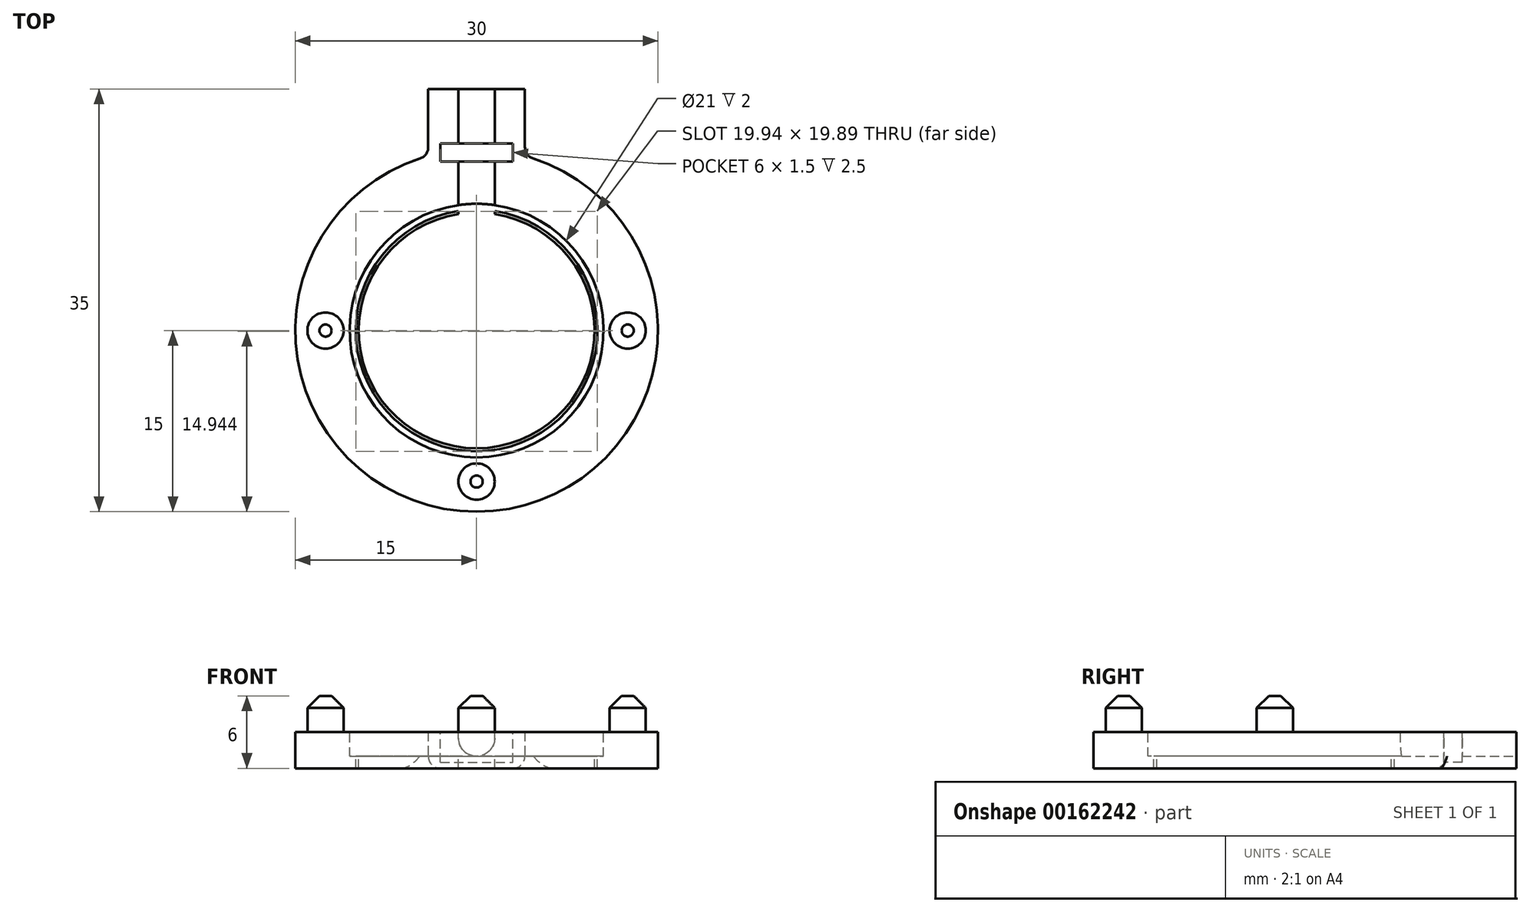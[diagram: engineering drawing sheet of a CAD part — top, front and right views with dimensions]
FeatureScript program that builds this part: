
annotation { "Feature Type Name" : "Feature", "Feature Type Description" : "" }
export const myFeature = defineFeature(function(context is Context, id is Id, definition is map)
    precondition{}
    {
        {
            var Q0;
            Q0=qCreatedBy(makeId("Top.planeOp"),FACE);
            var sketch = newSketch(context, id + "F0", { "sketchPlane" : qUnion([Q0])});
            skArc(sketch, "E0", {"start": v(-4, 14.46) * mm, "mid": v(0, -15) * mm, "end": v(4, 14.46) * mm});
            skLineSegment(sketch, "E1.bottom", {"start": v(-4, 20) * mm, "end": v(4, 20) * mm});
            skLineSegment(sketch, "E1.left", {"start": v(-4, 20) * mm, "end": v(-4, 14.46) * mm});
            skLineSegment(sketch, "E1.right", {"start": v(4, 20) * mm, "end": v(4, 14.46) * mm});
            skSolve(sketch);
        }
        {
            var Q0;
            Q0 = qSketchRegion(id + "F0", true);
            extrude(context, id + "F1", {"entities" : qUnion([Q0]), "depth" : 3 * mm});
        }
        {
            var Q0;
            Q0=makeQuery(id+"F1.opExtrude","CAP_FACE",FACE,{"disambiguationData":[OSD([sQuery(id+"F0.wireOp",EDGE,"E0"),sQuery(id+"F0.wireOp",EDGE,"E1.bottom"),sQuery(id+"F0.wireOp",EDGE,"E1.left"),sQuery(id+"F0.wireOp",EDGE,"E1.right")])],"isStart":false});
            var sketch = newSketch(context, id + "F2", { "sketchPlane" : qUnion([Q0])});
            skLineSegment(sketch, "E2.bottom", {"start": v(-1.5, 20) * mm, "end": v(1.5, 20) * mm});
            skLineSegment(sketch, "E2.left", {"start": v(-1.5, 20) * mm, "end": v(-1.5, 10.4) * mm});
            skLineSegment(sketch, "E2.right", {"start": v(1.5, 20) * mm, "end": v(1.5, 10.4) * mm});
            skArc(sketch, "E3", {"start": v(-1.5, 10.4) * mm, "mid": v(0, -10.5) * mm, "end": v(1.5, 10.4) * mm});
            skPoint(sketch, "E4.orphan", {"position": v(1.5, 8.67) * mm});
            skSolve(sketch);
        }
        {
            var Q0;
            Q0 = qSketchRegion(id + "F2", true);
            extrude(context, id + "F3", {"entities" : qUnion([Q0]), "operationType" : NewBodyOperationType.REMOVE, "oppositeDirection" : true, "depth" : 2 * mm});
        }
        {
            var Q0;
            Q0=makeQuery(id+"F1.opExtrude","CAP_FACE",FACE,{"disambiguationData":[OSD([sQuery(id+"F0.wireOp",EDGE,"E0"),sQuery(id+"F0.wireOp",EDGE,"E1.bottom"),sQuery(id+"F0.wireOp",EDGE,"E1.left"),sQuery(id+"F0.wireOp",EDGE,"E1.right")])],"isStart":false});
            var sketch = newSketch(context, id + "F4", { "sketchPlane" : qUnion([Q0])});
            skCircle(sketch, "E5", {"center": v(12.5, 0) * mm, "radius": 1.5 * mm});
            skCircle(sketch, "E6", {"center": v(-12.5, 0) * mm, "radius": 1.5 * mm});
            skCircle(sketch, "E7", {"center": v(0, -12.5) * mm, "radius": 1.5 * mm});
            skSolve(sketch);
        }
        {
            var Q0;
            Q0 = qSketchRegion(id + "F4", true);
            extrude(context, id + "F5", {"entities" : qUnion([Q0]), "operationType" : NewBodyOperationType.ADD, "depth" : 3 * mm});
        }
        {
            var Q0;
            Q0=makeQuery(id+"F5.opExtrude","CAP_EDGE",EDGE,{"disambiguationData":[OSD([sQuery(id+"F4.wireOp",EDGE,"E6")])],"isStart":false});
            var Q1;
            Q1=makeQuery(id+"F5.opExtrude","CAP_EDGE",EDGE,{"disambiguationData":[OSD([sQuery(id+"F4.wireOp",EDGE,"E7")])],"isStart":false});
            var Q2;
            Q2=makeQuery(id+"F5.opExtrude","CAP_EDGE",EDGE,{"disambiguationData":[OSD([sQuery(id+"F4.wireOp",EDGE,"E5")])],"isStart":false});
            chamfer(context, id + "F6", {"entities" : qUnion([Q0, Q1, Q2]), "width" : 1 * mm, "tangentPropagation" : true});
        }
        {
            var Q0;
            Q0=makeQuery(id+"F1.opExtrude","CAP_EDGE",EDGE,{"disambiguationData":[OSD([sQuery(id+"F0.wireOp",EDGE,"E1.right")])],"isStart":true});
            var Q1;
            Q1=makeQuery(id+"F1.opExtrude","SWEPT_EDGE",EDGE,{"disambiguationData":[OSD([sQuery(id+"F0.wireOp",EDGE,"E0"),sQuery(id+"F0.wireOp",EDGE,"E1.right")])]});
            var Q2;
            Q2=makeQuery(id+"F1.opExtrude","SWEPT_EDGE",EDGE,{"disambiguationData":[OSD([sQuery(id+"F0.wireOp",EDGE,"E0"),sQuery(id+"F0.wireOp",EDGE,"E1.left")])]});
            var Q3;
            Q3=makeQuery(id+"F1.opExtrude","CAP_EDGE",EDGE,{"disambiguationData":[OSD([sQuery(id+"F0.wireOp",EDGE,"E1.left")])],"isStart":true});
            fillet(context, id + "F7", {"entities" : qUnion([Q0, Q1, Q2, Q3]), "radius" : 1 * mm, "tangentPropagation" : true, "allowEdgeOverflow" : false});
        }
        {
            var Q0;
            Q0=makeQuery(id+"F3.boolean.opBoolean","COPY",FACE,{"derivedFrom":makeQuery(id+"F3.opExtrude","CAP_FACE",FACE,{"disambiguationData":[OSD([sQuery(id+"F2.wireOp",EDGE,"E2.bottom"),sQuery(id+"F2.wireOp",EDGE,"E2.left"),sQuery(id+"F2.wireOp",EDGE,"E2.right"),sQuery(id+"F2.wireOp",EDGE,"E3")])],"isStart":false})});
            var sketch = newSketch(context, id + "F8", { "sketchPlane" : qUnion([Q0])});
            skArc(sketch, "E8", {"start": v(-1.5, 9.89) * mm, "mid": v(0, -10) * mm, "end": v(1.5, 9.89) * mm});
            skArc(sketch, "E9", {"start": v(-1.5, 9.63) * mm, "mid": v(0, -9.75) * mm, "end": v(1.5, 9.63) * mm});
            skLineSegment(sketch, "E10.left", {"start": v(-1.5, 9.89) * mm, "end": v(-1.5, 9.63) * mm});
            skLineSegment(sketch, "E10.right", {"start": v(1.5, 9.89) * mm, "end": v(1.5, 9.63) * mm});
            skPoint(sketch, "E11.orphan", {"position": v(1.5, 7.73) * mm});
            skSolve(sketch);
        }
        {
            var Q0;
            Q0 = qSketchRegion(id + "F8", true);
            extrude(context, id + "F9", {"entities" : qUnion([Q0]), "operationType" : NewBodyOperationType.REMOVE, "endBound" : BoundingType.THROUGH_ALL, "oppositeDirection" : true, "depth" : 25 * mm});
        }
        {
            var Q0;
            Q0=makeQuery(id+"F3.boolean.opBoolean","COPY",EDGE,{"derivedFrom":makeQuery(id+"F3.opExtrude","CAP_EDGE",EDGE,{"disambiguationData":[OSD([sQuery(id+"F2.wireOp",EDGE,"E2.right")])],"isStart":false})});
            var Q1;
            Q1=makeQuery(id+"F3.boolean.opBoolean","COPY",EDGE,{"derivedFrom":makeQuery(id+"F3.opExtrude","CAP_EDGE",EDGE,{"disambiguationData":[OSD([sQuery(id+"F2.wireOp",EDGE,"E2.left")])],"isStart":false})});
            fillet(context, id + "F10", {"entities" : qUnion([Q0, Q1]), "radius" : 1.5 * mm, "tangentPropagation" : true, "allowEdgeOverflow" : false});
        }
        {
            var Q0;
            Q0=makeQuery(id+"F1.opExtrude","CAP_FACE",FACE,{"disambiguationData":[OSD([sQuery(id+"F0.wireOp",EDGE,"E0"),sQuery(id+"F0.wireOp",EDGE,"E1.bottom"),sQuery(id+"F0.wireOp",EDGE,"E1.left"),sQuery(id+"F0.wireOp",EDGE,"E1.right")])],"isStart":false});
            var sketch = newSketch(context, id + "F11", { "sketchPlane" : qUnion([Q0])});
            skLineSegment(sketch, "E12.bottom", {"start": v(-3, 15.5) * mm, "end": v(3, 15.5) * mm});
            skLineSegment(sketch, "E12.top", {"start": v(-3, 14) * mm, "end": v(3, 14) * mm});
            skLineSegment(sketch, "E12.left", {"start": v(-3, 15.5) * mm, "end": v(-3, 14) * mm});
            skLineSegment(sketch, "E12.right", {"start": v(3, 15.5) * mm, "end": v(3, 14) * mm});
            skSolve(sketch);
        }
        {
            var Q0;
            Q0 = qSketchRegion(id + "F11", true);
            extrude(context, id + "F12", {"entities" : qUnion([Q0]), "operationType" : NewBodyOperationType.REMOVE, "oppositeDirection" : true, "depth" : 2.5 * mm});
        }
    });
